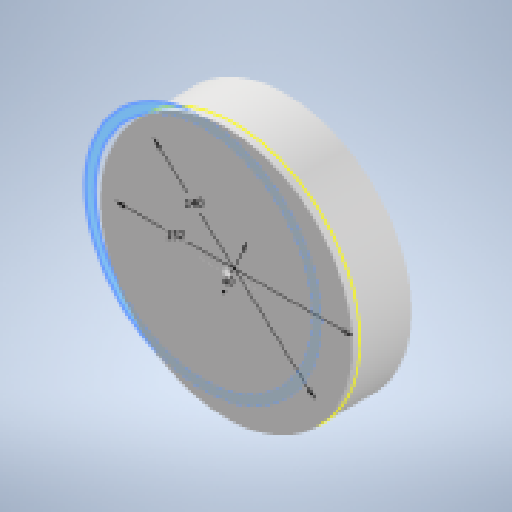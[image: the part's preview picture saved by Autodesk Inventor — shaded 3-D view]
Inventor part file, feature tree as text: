
AUTODESK INVENTOR PART (.ipt)
format: ipt  version: 2025 (Build 290162010, 162A)  size: 181,760 bytes
history: native  units: mm
features: reference x6, extrude x3, sketch x3, hole x3, other x3, projected_geometry x1
ambient origin geometry x8: Origin, YZ Plane, XZ Plane, XY Plane, X Axis, Y Axis, Z Axis, Center Point
bodies: Volumenkörper1 (feature_tree)
feature tree (19):
  extrude  "Extrusion1"  Depth=5.0mm TaperAngle=0.0deg
  sketch  "Skizze2"  dims[d3=140.0mm d4=40.0mm]
  hole  "Bohrung1"  [1 undecoded]
  extrude  "Extrusion2"  Depth=2.5mm TaperAngle=0.0deg
  hole  "Bohrung2"  [1 undecoded]
  extrude  "Extrusion3"  Depth=33.0mm TaperAngle=0.0deg
  hole  "Bohrung3"  [1 undecoded]
  sketch  "Skizze1"  dims[d0=162.0mm d1=5.0mm d2=0.0mm]
  projected_geometry  "Projizierte Kontur1"
  sketch  "Skizze3"  dims[d5=5.0mm d6=6.0mm d7=4.0mm d8=2.0mm d9=90.0deg d10=8.0mm d11=20.594885mm d12=2.5mm d13=0.0mm d14=0.7mm d15=6.0mm d16=4.0mm d17=2.0mm d18=90.0deg d19=8.0mm d20=20.594885mm d21=152.0mm d22=33.0mm d23=0.0mm d24=0.929367mm d25=2.4mm d26=4.4mm d27=2.0mm d28=90.0deg d29=10.0mm d30=20.594885mm]
  reference  "Referenz1"
  reference  "Referenz2"
  reference  "Referenz3"
  reference  "Referenz4"
  reference  "Referenz5"
  reference  "Referenz6"
  other  "<userpath>\GIT\pillbox\Baugruppe1.iam"
  other  "Baugruppe1.iam"
  other  "Bauteil3:1"
note: 3 required parameter values undecoded (feature->parameter linkage not recoverable at this tier; creation-order binding heuristic only, values carry confidence <= 0.55)
